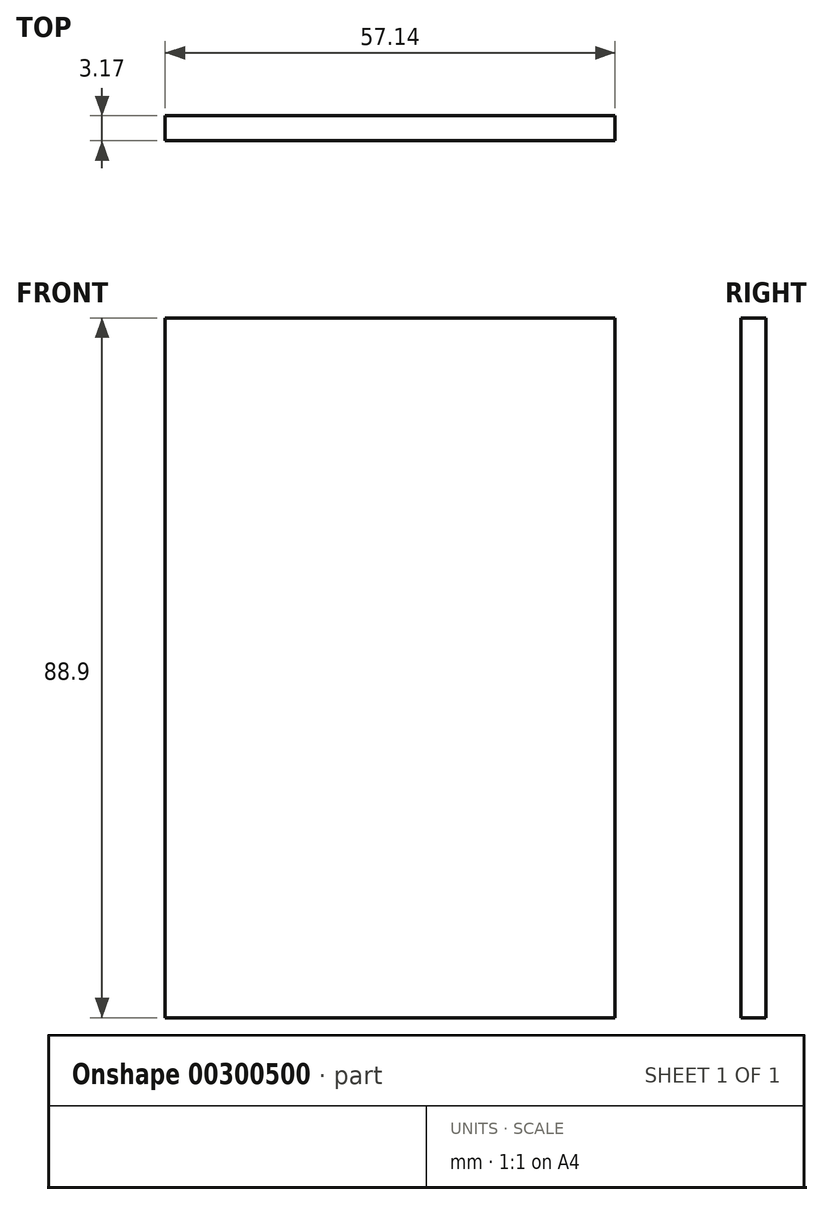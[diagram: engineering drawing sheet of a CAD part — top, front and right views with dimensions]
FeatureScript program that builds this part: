
annotation { "Feature Type Name" : "Feature", "Feature Type Description" : "" }
export const myFeature = defineFeature(function(context is Context, id is Id, definition is map)
    precondition{}
    {
        {
            var Q0;
            Q0=qCreatedBy(makeId("Front.planeOp"),FACE);
            var sketch = newSketch(context, id + "F0", { "sketchPlane" : qUnion([Q0])});
            skLineSegment(sketch, "E0.bottom", {"start": v(-28.57, 44.45) * mm, "end": v(28.58, 44.45) * mm});
            skLineSegment(sketch, "E0.top", {"start": v(-28.58, -44.45) * mm, "end": v(28.58, -44.45) * mm});
            skLineSegment(sketch, "E0.left", {"start": v(-28.57, 44.45) * mm, "end": v(-28.57, -44.45) * mm});
            skLineSegment(sketch, "E0.right", {"start": v(28.58, 44.45) * mm, "end": v(28.58, -44.45) * mm});
            skPoint(sketch, "E0.middle", {"position": v(0, 0) * mm});
            skSolve(sketch);
        }
        {
            var Q0;
            Q0 = qSketchRegion(id + "F0", true);
            extrude(context, id + "F1", {"entities" : qUnion([Q0]), "depth" : 3.17 * mm});
        }
    });
